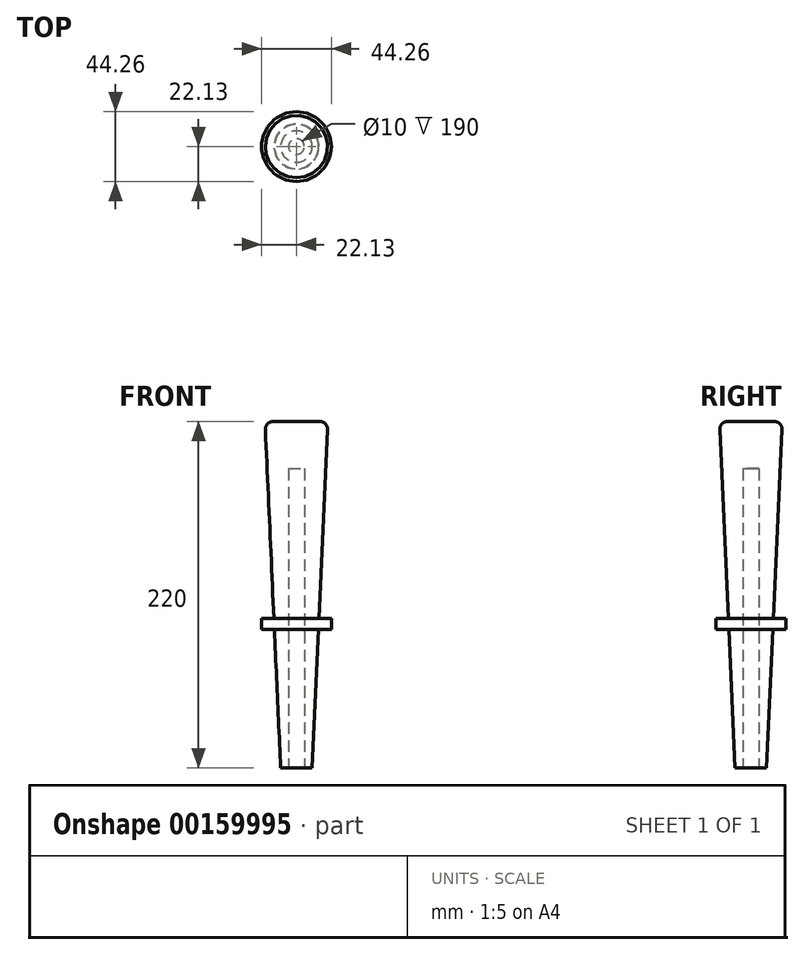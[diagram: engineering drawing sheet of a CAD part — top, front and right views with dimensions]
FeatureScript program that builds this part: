
annotation { "Feature Type Name" : "Feature", "Feature Type Description" : "" }
export const myFeature = defineFeature(function(context is Context, id is Id, definition is map)
    precondition{}
    {
        {
            var Q0;
            Q0=qCreatedBy(makeId("Front.planeOp"),FACE);
            var sketch = newSketch(context, id + "F0", { "sketchPlane" : qUnion([Q0])});
            skLineSegment(sketch, "E0", {"start": v(-5, 0) * mm, "end": v(-10, 0) * mm});
            skLineSegment(sketch, "E1", {"start": v(-10, 0) * mm, "end": v(-14, 87.78) * mm});
            skLineSegment(sketch, "E2", {"start": v(-14.77, 220) * mm, "end": v(0, 220) * mm});
            skLineSegment(sketch, "E3", {"start": v(-5, 0) * mm, "end": v(-5, 190) * mm});
            skLineSegment(sketch, "E4", {"start": v(-5, 190) * mm, "end": v(0, 190) * mm});
            skLineSegment(sketch, "E5", {"start": v(0, 190) * mm, "end": v(0, 220) * mm});
            skPoint(sketch, "E6.orphan", {"position": v(0, 0) * mm});
            skPoint(sketch, "E7.visualSharp", {"position": v(-20, 220) * mm});
            skArc(sketch, "E7.filletArc", {"start": v(-14.77, 220) * mm, "mid": v(-18.38, 218.45) * mm, "end": v(-19.76, 214.77) * mm});
            skLineSegment(sketch, "E8", {"start": v(0, 0) * mm, "end": v(0, 271.28) * mm, "construction": true});
            skLineSegment(sketch, "E9.bottom", {"start": v(-14.32, 95) * mm, "end": v(-22.13, 95) * mm});
            skLineSegment(sketch, "E9.top", {"start": v(-14, 87.78) * mm, "end": v(-22.13, 87.78) * mm});
            skLineSegment(sketch, "E9.left", {"start": v(-5, 95) * mm, "end": v(-5, 87.78) * mm});
            skLineSegment(sketch, "E9.right", {"start": v(-22.13, 95) * mm, "end": v(-22.13, 87.78) * mm});
            skLineSegment(sketch, "E10.trimOffspring", {"start": v(-14.32, 95) * mm, "end": v(-19.76, 214.77) * mm});
            skSolve(sketch);
        }
        {
            var Q0;
            Q0=makeQuery(id+"F0.imprint","IMPRINT",FACE,{"disambiguationData":[TD([[makeQuery(id+"F0.imprint","IMPRINT",EDGE,{"derivedFrom":sQuery(id+"F0.wireOp",EDGE,"E0")}),-1.0]])]});
            var Q1;
            Q1=sQuery(id+"F0.wireOp",EDGE,"E8");
            revolve(context, id + "F1", {"entities" : qUnion([Q0]), "axis" : qUnion([Q1]), "revolveType" : RevolveType.FULL});
        }
    });
